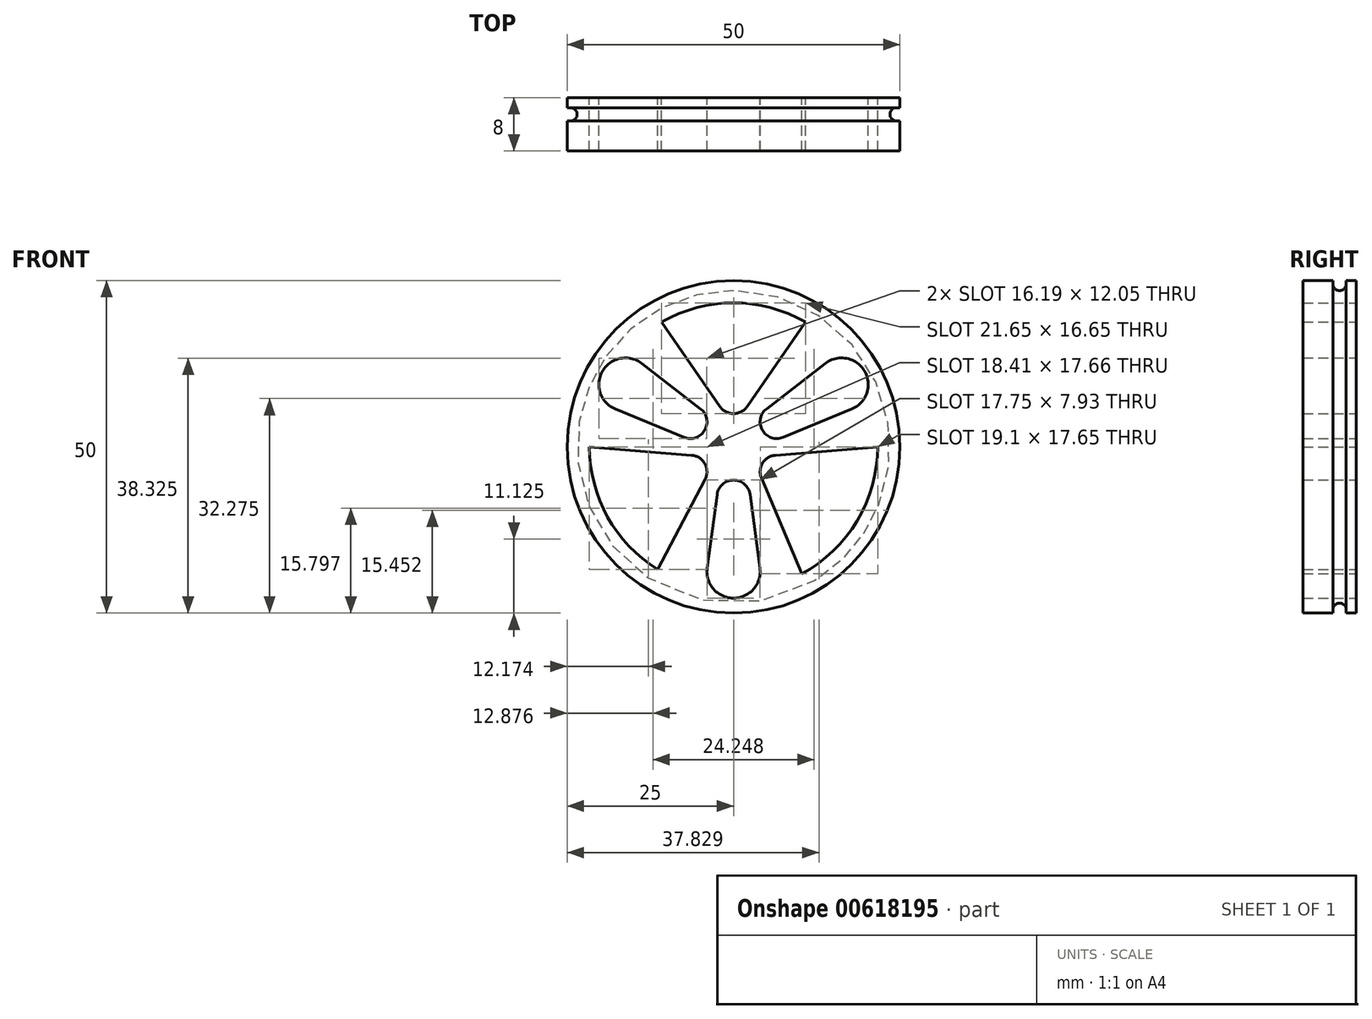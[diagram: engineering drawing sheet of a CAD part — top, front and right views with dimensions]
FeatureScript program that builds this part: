
annotation { "Feature Type Name" : "Feature", "Feature Type Description" : "" }
export const myFeature = defineFeature(function(context is Context, id is Id, definition is map)
    precondition{}
    {
        {
            var Q0;
            Q0=qCreatedBy(makeId("Front.planeOp"),FACE);
            var sketch = newSketch(context, id + "F0", { "sketchPlane" : qUnion([Q0])});
            skCircle(sketch, "E0", {"center": v(0, 0) * mm, "radius": 25 * mm});
            skCircle(sketch, "E1", {"center": v(0, 0) * mm, "radius": 12.5 * mm, "construction": true});
            skCircle(sketch, "E2.cCircle", {"center": v(0, 0) * mm, "radius": 25 * mm, "construction": true});
            skLineSegment(sketch, "E2.0", {"start": v(0, 25) * mm, "end": v(21.65, 12.5) * mm, "construction": true});
            skLineSegment(sketch, "E2.1", {"start": v(21.65, 12.5) * mm, "end": v(21.65, -12.5) * mm, "construction": true});
            skLineSegment(sketch, "E2.2", {"start": v(21.65, -12.5) * mm, "end": v(0, -25) * mm, "construction": true});
            skLineSegment(sketch, "E2.3", {"start": v(0, -25) * mm, "end": v(-21.65, -12.5) * mm, "construction": true});
            skLineSegment(sketch, "E2.4", {"start": v(-21.65, -12.5) * mm, "end": v(-21.65, 12.5) * mm, "construction": true});
            skLineSegment(sketch, "E2.5", {"start": v(-21.65, 12.5) * mm, "end": v(0, 25) * mm, "construction": true});
            skLineSegment(sketch, "E3", {"start": v(-21.65, 12.5) * mm, "end": v(0, 0) * mm, "construction": true});
            skLineSegment(sketch, "E4", {"start": v(0, 25) * mm, "end": v(0, 0) * mm, "construction": true});
            skLineSegment(sketch, "E5", {"start": v(0, 0) * mm, "end": v(-21.65, -12.5) * mm, "construction": true});
            skLineSegment(sketch, "E6", {"start": v(0, -25) * mm, "end": v(0, 0) * mm, "construction": true});
            skLineSegment(sketch, "E7", {"start": v(0, 0) * mm, "end": v(25, 0) * mm, "construction": true});
            skLineSegment(sketch, "E8", {"start": v(21.65, 12.5) * mm, "end": v(0, 0) * mm, "construction": true});
            skLineSegment(sketch, "E9", {"start": v(0, 0) * mm, "end": v(21.65, -12.5) * mm, "construction": true});
            skCircle(sketch, "E10", {"center": v(0, 0) * mm, "radius": 18.75 * mm, "construction": true});
            skLineSegment(sketch, "E11.0", {"start": v(18.75, 0) * mm, "end": v(9.38, -16.24) * mm, "construction": true});
            skLineSegment(sketch, "E11.1", {"start": v(9.38, -16.24) * mm, "end": v(-9.37, -16.24) * mm, "construction": true});
            skLineSegment(sketch, "E11.2", {"start": v(-9.37, -16.24) * mm, "end": v(-18.75, 0) * mm, "construction": true});
            skLineSegment(sketch, "E11.3", {"start": v(-18.75, 0) * mm, "end": v(-9.38, 16.24) * mm, "construction": true});
            skLineSegment(sketch, "E11.4", {"start": v(-9.38, 16.24) * mm, "end": v(9.37, 16.24) * mm, "construction": true});
            skLineSegment(sketch, "E11.5", {"start": v(9.37, 16.24) * mm, "end": v(18.75, 0) * mm, "construction": true});
            skCircle(sketch, "E12", {"center": v(0, 0) * mm, "radius": 7.5 * mm, "construction": true});
            skCircle(sketch, "E13", {"center": v(-6.5, 3.75) * mm, "radius": 2.5 * mm});
            skCircle(sketch, "E14", {"center": v(0, 7.5) * mm, "radius": 2.5 * mm});
            skCircle(sketch, "E15", {"center": v(6.5, 3.75) * mm, "radius": 2.5 * mm});
            skCircle(sketch, "E16", {"center": v(6.5, -3.75) * mm, "radius": 2.5 * mm});
            skCircle(sketch, "E17", {"center": v(-6.5, -3.75) * mm, "radius": 2.5 * mm});
            skCircle(sketch, "E18", {"center": v(0, -7.5) * mm, "radius": 2.5 * mm});
            skLineSegment(sketch, "E19", {"start": v(-21.65, 12.5) * mm, "end": v(-10.83, 18.75) * mm, "construction": true});
            skLineSegment(sketch, "E20", {"start": v(-10.83, 18.75) * mm, "end": v(-2.06, 6.08) * mm});
            skLineSegment(sketch, "E21", {"start": v(10.83, 18.75) * mm, "end": v(2.06, 6.08) * mm});
            skArc(sketch, "E22", {"start": v(10.83, 18.75) * mm, "mid": v(0, 21.65) * mm, "end": v(-10.83, 18.75) * mm});
            skLineSegment(sketch, "E23", {"start": v(-21.66, 0) * mm, "end": v(-6.3, -1.26) * mm});
            skLineSegment(sketch, "E24", {"start": v(-11.42, -18.4) * mm, "end": v(-4.29, -4.92) * mm});
            skArc(sketch, "E25.trimOffspring", {"start": v(10.23, -19.1) * mm, "mid": v(18.7, -10.92) * mm, "end": v(21.65, 0.48) * mm});
            skArc(sketch, "E26.trimOffspring", {"start": v(-21.65, 0.48) * mm, "mid": v(-18.7, -10.92) * mm, "end": v(-10.23, -19.1) * mm});
            skLineSegment(sketch, "E27", {"start": v(10.23, -19.1) * mm, "end": v(3.31, -2.63) * mm});
            skLineSegment(sketch, "E28", {"start": v(21.66, 0) * mm, "end": v(4.4, -1.41) * mm});
            skCircle(sketch, "E29", {"center": v(-16.24, 9.37) * mm, "radius": 4 * mm});
            skLineSegment(sketch, "E30", {"start": v(-4.57, 0.26) * mm, "end": v(-22.3, 7.54) * mm});
            skLineSegment(sketch, "E31", {"start": v(-16.14, 14.35) * mm, "end": v(-2.94, 4.17) * mm});
            skCircle(sketch, "E32", {"center": v(16.24, 9.38) * mm, "radius": 4 * mm});
            skCircle(sketch, "E33", {"center": v(0, -18.75) * mm, "radius": 4 * mm});
            skLineSegment(sketch, "E34", {"start": v(-4.38, -21.3) * mm, "end": v(-2.15, -4.71) * mm});
            skLineSegment(sketch, "E35", {"start": v(4.37, -21.2) * mm, "end": v(2.18, -4.93) * mm});
            skLineSegment(sketch, "E36", {"start": v(20.58, 6.84) * mm, "end": v(5.63, 0.7) * mm});
            skLineSegment(sketch, "E37", {"start": v(2.95, 4.17) * mm, "end": v(15.4, 13.77) * mm});
            skSolve(sketch);
        }
        {
            var Q0;
            Q0=makeQuery(id+"F0.imprint","IMPRINT",FACE,{"disambiguationData":[TD([[makeQuery(id+"F0.imprint","IMPRINT",EDGE,{"derivedFrom":sQuery(id+"F0.wireOp",EDGE,"E0")}),1.0]])]});
            extrude(context, id + "F1", {"entities" : qUnion([Q0]), "depth" : 8 * mm, "offsetDistance" : 25 * mm});
        }
        {
            var Q0;
            Q0=makeQuery(id+"F1.opExtrude","CAP_FACE",FACE,{"disambiguationData":[OSD([sQuery(id+"F0.wireOp",EDGE,"E0"),sQuery(id+"F0.wireOp",EDGE,"Z6RS1KqU-DIUb-8x9t-4Cod-346lC7Tq3F3O"),sQuery(id+"F0.wireOp",EDGE,"u6Au5P1E-UY6F-NhHg-ce26-Ah4b0uqlgmlL"),sQuery(id+"F0.wireOp",EDGE,"1c3DNsgp-pRrH-Oyov-zOWk-DgdX0Lu4QuXT"),sQuery(id+"F0.wireOp",EDGE,"HJVHzOqU-uWk6-I98U-JFDy-MPg3AoAM1DtL"),sQuery(id+"F0.wireOp",EDGE,"2pv1tVm9-dUXk-2eVU-Eova-xsGhsFCM7xaJ"),sQuery(id+"F0.wireOp",EDGE,"ANuxtUcM-mjTO-lXoG-hyGZ-zmeMgCLTGJ9E"),sQuery(id+"F0.wireOp",EDGE,"pKtygAKV-84Ui-JhgS-Bppe-Dj3IemfIFeSI"),sQuery(id+"F0.wireOp",EDGE,"uQ2lF8QX-CVbW-0OL5-L041-3Fc2WnX4qEB0"),sQuery(id+"F0.wireOp",EDGE,"khzvo0Hp-LspV-69yB-DEYR-88Vc2yCnbkfe"),sQuery(id+"F0.wireOp",EDGE,"eTCysbWw-EX7z-NPcg-lpeu-3eAoNfMLjMyn"),sQuery(id+"F0.wireOp",EDGE,"ySNWszwt-60gd-okuN-xFbG-CCWbGH4mVSbJ"),sQuery(id+"F0.wireOp",EDGE,"22rZnsJL-nDAh-GeAM-JxOs-SZYcAvOiCNFL")])],"isStart":false});
            cPlane(context, id + "F2", {"entities" : qUnion([Q0]), "cplaneType" : CPlaneType.OFFSET, "offset" : 2.5 * mm, "oppositeDirection" : true, "width" : 150 * mm, "height" : 150 * mm});
        }
        {
            var Q0;
            Q0=qCreatedBy(makeId("Right.planeOp"),FACE);
            var sketch = newSketch(context, id + "F3", { "sketchPlane" : qUnion([Q0])});
            skLineSegment(sketch, "E38", {"start": v(0, 0) * mm, "end": v(0, 25) * mm, "construction": true});
            skLineSegment(sketch, "E39", {"start": v(0, 25) * mm, "end": v(-5, 25) * mm, "construction": true});
            skLineSegment(sketch, "E40", {"start": v(0, 25) * mm, "end": v(-1.5, 25) * mm, "construction": true});
            skLineSegment(sketch, "E41", {"start": v(-1.63, 25) * mm, "end": v(-2, 25) * mm, "construction": true});
            skLineSegment(sketch, "E42.left", {"start": v(-3.5, 23.5) * mm, "end": v(-3.5, 25) * mm});
            skLineSegment(sketch, "E42.right", {"start": v(-1.5, 23.5) * mm, "end": v(-1.5, 25) * mm});
            skLineSegment(sketch, "E43", {"start": v(-3.5, 23.5) * mm, "end": v(-1.5, 25.5) * mm, "construction": true});
            skLineSegment(sketch, "E44", {"start": v(-1.5, 23.5) * mm, "end": v(-3.5, 25.5) * mm, "construction": true});
            skCircle(sketch, "E45", {"center": v(-2.5, 24.5) * mm, "radius": 1 * mm});
            skLineSegment(sketch, "E46", {"start": v(-3.5, 25) * mm, "end": v(-3.5, 23.5) * mm});
            skLineSegment(sketch, "E47", {"start": v(-3.5, 25) * mm, "end": v(-1.5, 25) * mm});
            skLineSegment(sketch, "E48", {"start": v(-3.5, 23.5) * mm, "end": v(-3.5, 25.5) * mm});
            skLineSegment(sketch, "E49.trimOffspring", {"start": v(-3, 25) * mm, "end": v(-3.5, 25) * mm, "construction": true});
            skSolve(sketch);
        }
        {
            var Q0;
            Q0=qCreatedBy(makeId("Top.planeOp"),FACE);
            var sketch = newSketch(context, id + "F4", { "sketchPlane" : qUnion([Q0])});
            skLineSegment(sketch, "E50", {"start": v(0, 0) * mm, "end": v(0, -5) * mm, "construction": true});
            skSolve(sketch);
        }
        {
            var Q0;
            Q0=qSketchRegion(id+"F3",true);
            var Q1;
            Q1=sQuery(id+"F4.wireOp",EDGE,"E50");
            revolve(context, id + "F5", {"operationType" : NewBodyOperationType.REMOVE, "entities" : qUnion([Q0]), "axis" : qUnion([Q1]), "revolveType" : RevolveType.FULL});
        }
    });
